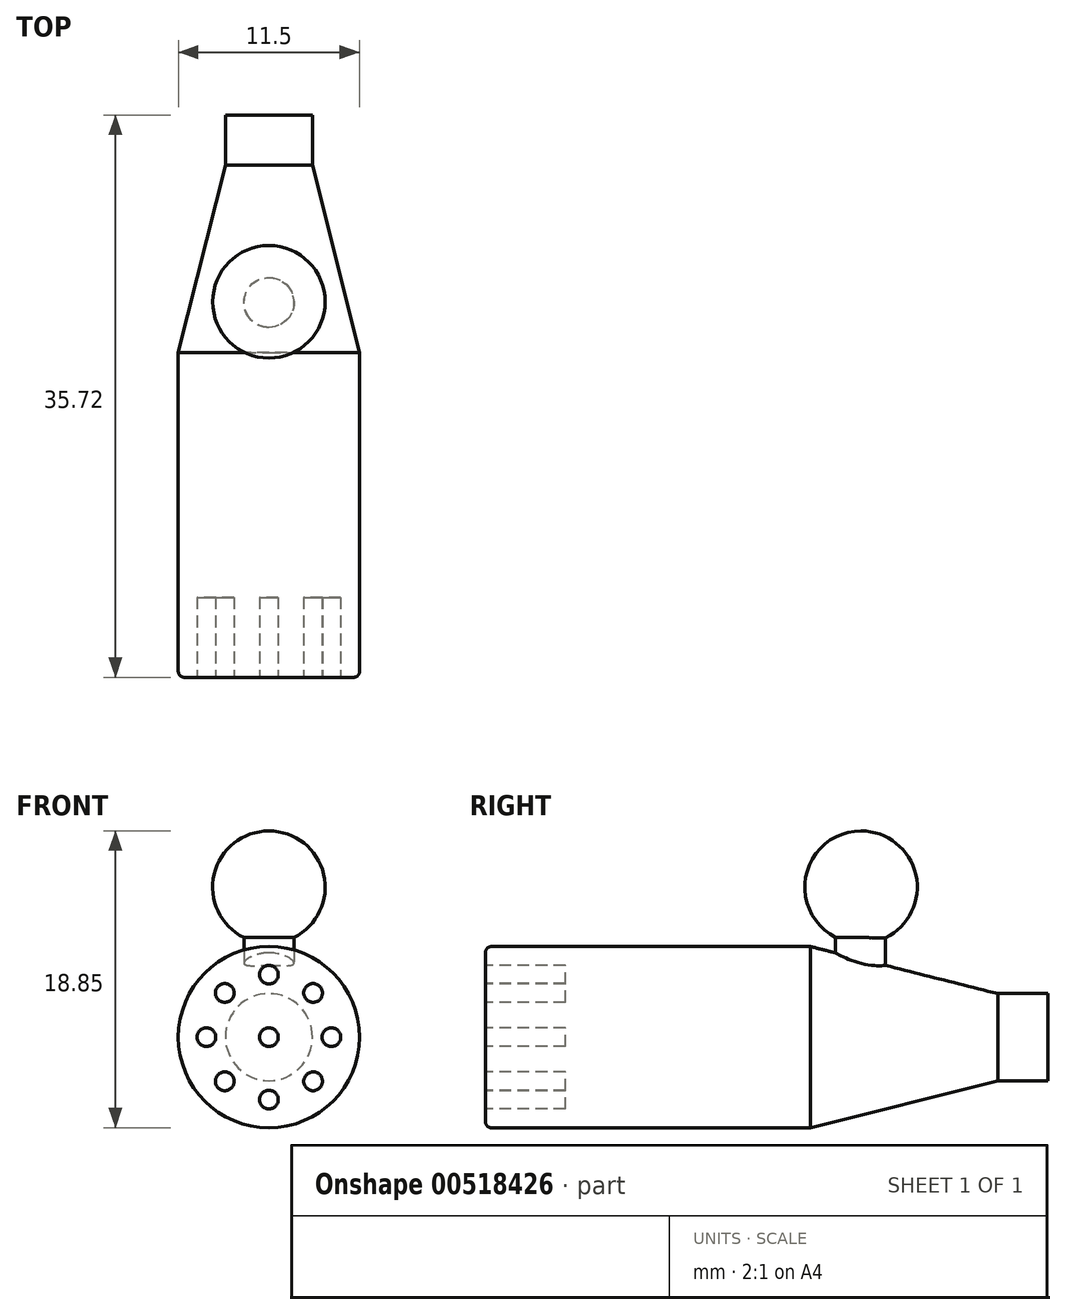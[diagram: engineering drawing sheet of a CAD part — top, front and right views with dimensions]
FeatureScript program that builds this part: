
annotation { "Feature Type Name" : "Feature", "Feature Type Description" : "" }
export const myFeature = defineFeature(function(context is Context, id is Id, definition is map)
    precondition{}
    {
        {
            var Q0;
            Q0=qCreatedBy(makeId("Front.planeOp"),FACE);
            var sketch = newSketch(context, id + "F0", { "sketchPlane" : qUnion([Q0])});
            skCircle(sketch, "E0", {"center": v(0, 0) * mm, "radius": 5.75 * mm});
            skSolve(sketch);
        }
        {
            var Q0;
            Q0 = qSketchRegion(id + "F0", true);
            extrude(context, id + "F1", {"entities" : qUnion([Q0]), "depth" : 20.64 * mm, "offsetDistance" : 25.4 * mm});
        }
        {
            var Q0;
            Q0=makeQuery(id+"F1.opExtrude","CAP_FACE",FACE,{"disambiguationData":[OSD([sQuery(id+"F0.wireOp",EDGE,"E0")])],"isStart":true});
            var sketch = newSketch(context, id + "F2", { "sketchPlane" : qUnion([Q0])});
            skCircle(sketch, "E1.0", {"center": v(0, 0) * mm, "radius": 5.75 * mm});
            skSolve(sketch);
        }
        {
            var Q0;
            Q0 = qSketchRegion(id + "F2", true);
            extrude(context, id + "F3", {"entities" : qUnion([Q0]), "operationType" : NewBodyOperationType.ADD, "depth" : 11.9 * mm, "offsetDistance" : 25.4 * mm, "hasDraft" : true, "draftAngle" : 14.1 * degree, "draftPullDirection" : true});
        }
        {
            var Q0;
            Q0=makeQuery(id+"F3.opExtrude","CAP_FACE",FACE,{"disambiguationData":[OSD([sQuery(id+"F2.wireOp",EDGE,"E1.0")])],"isStart":false});
            var sketch = newSketch(context, id + "F4", { "sketchPlane" : qUnion([Q0])});
            skCircle(sketch, "E2.0", {"center": v(0, 0) * mm, "radius": 2.76 * mm});
            skSolve(sketch);
        }
        {
            var Q0;
            Q0 = qSketchRegion(id + "F4", true);
            extrude(context, id + "F5", {"entities" : qUnion([Q0]), "operationType" : NewBodyOperationType.ADD, "depth" : 3.17 * mm, "offsetDistance" : 25.4 * mm});
        }
        {
            var Q0;
            Q0=makeQuery(id+"F1.opExtrude","CAP_FACE",FACE,{"disambiguationData":[OSD([sQuery(id+"F0.wireOp",EDGE,"E0")])],"isStart":false});
            var sketch = newSketch(context, id + "F6", { "sketchPlane" : qUnion([Q0])});
            skCircle(sketch, "E3", {"center": v(0, 0) * mm, "radius": 0.6 * mm});
            skCircle(sketch, "E4", {"center": v(0, 3.97) * mm, "radius": 0.6 * mm});
            skCircle(sketch, "E5.1.0", {"center": v(-2.8, 2.8) * mm, "radius": 0.6 * mm});
            skCircle(sketch, "E5.2.0", {"center": v(-3.97, 0) * mm, "radius": 0.6 * mm});
            skCircle(sketch, "E5.3.0", {"center": v(-2.8, -2.8) * mm, "radius": 0.6 * mm});
            skCircle(sketch, "E5.4.0", {"center": v(0, -3.97) * mm, "radius": 0.6 * mm});
            skCircle(sketch, "E5.5.0", {"center": v(2.8, -2.8) * mm, "radius": 0.6 * mm});
            skCircle(sketch, "E5.6.0", {"center": v(3.97, 0) * mm, "radius": 0.6 * mm});
            skCircle(sketch, "E5.7.0", {"center": v(2.8, 2.8) * mm, "radius": 0.6 * mm});
            skSolve(sketch);
        }
        {
            var Q0;
            Q0 = qSketchRegion(id + "F6", true);
            extrude(context, id + "F7", {"entities" : qUnion([Q0]), "operationType" : NewBodyOperationType.REMOVE, "oppositeDirection" : true, "depth" : 5.08 * mm, "offsetDistance" : 25.4 * mm});
        }
        {
            var Q0;
            Q0=makeQuery(id+"F1.opExtrude","CAP_EDGE",EDGE,{"disambiguationData":[OSD([sQuery(id+"F0.wireOp",EDGE,"E0")])],"isStart":false});
            fillet(context, id + "F8", {"entities" : qUnion([Q0]), "radius" : 0.38 * mm, "tangentPropagation" : true, "allowEdgeOverflow" : false});
        }
        {
            var Q0;
            Q0=qCreatedBy(makeId("Top.planeOp"),FACE);
            var sketch = newSketch(context, id + "F9", { "sketchPlane" : qUnion([Q0])});
            skCircle(sketch, "E6", {"center": v(0, 3.18) * mm, "radius": 1.59 * mm});
            skSolve(sketch);
        }
        {
            var Q0;
            Q0 = qSketchRegion(id + "F9", true);
            extrude(context, id + "F10", {"entities" : qUnion([Q0]), "operationType" : NewBodyOperationType.ADD, "depth" : 9.52 * mm, "offsetDistance" : 25.4 * mm});
        }
        {
            var Q0;
            Q0=qCreatedBy(makeId("Right.planeOp"),FACE);
            var sketch = newSketch(context, id + "F11", { "sketchPlane" : qUnion([Q0])});
            skArc(sketch, "E7", {"start": v(3.22, 5.95) * mm, "mid": v(6.79, 9.53) * mm, "end": v(3.22, 13.1) * mm});
            skLineSegment(sketch, "E8", {"start": v(3.22, 5.95) * mm, "end": v(3.22, 13.1) * mm});
            skSolve(sketch);
        }
        {
            var Q0;
            Q0=makeQuery(id+"F11.imprint","IMPRINT",FACE,{"disambiguationData":[TD([[makeQuery(id+"F11.imprint","IMPRINT",EDGE,{"derivedFrom":sQuery(id+"F11.wireOp",EDGE,"E7")}),1.0]])]});
            var Q1;
            Q1=sQuery(id+"F11.wireOp",EDGE,"E8");
            revolve(context, id + "F12", {"operationType" : NewBodyOperationType.ADD, "entities" : qUnion([Q0]), "axis" : qUnion([Q1]), "revolveType" : RevolveType.FULL});
        }
    });
